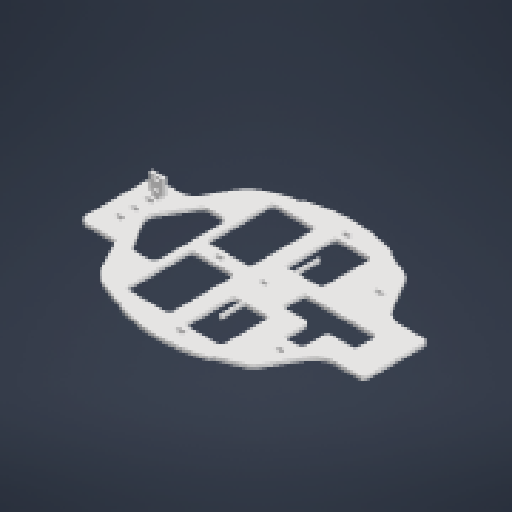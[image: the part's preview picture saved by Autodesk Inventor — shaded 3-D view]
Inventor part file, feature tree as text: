
AUTODESK INVENTOR PART (.ipt)
format: ipt  version: 2025.3 (Build 293356000, 356)  size: 523,264 bytes
history: native  units: in
note: dims shown in document units (in); Inventor stores cm internally (conversion verified against a paired STEP export)
features: extrude x3, sketch x2, projected_geometry x2, other x2, reference x1
ambient origin geometry x8: Origin, YZ Plane, XZ Plane, XY Plane, X Axis, Y Axis, Z Axis, Center Point
bodies: Solid1 (feature_tree), Solid2 (feature_tree), Body1 (feature_tree), Body2 (feature_tree)
feature tree (10):
  sketch  "Sketch1"  dims[d0=0.3937in d1=0.1969in]
  extrude  "Extrusion1"  Depth=0.1969in
  extrude  "Extrusion2"  Depth=0.3937in TaperAngle=0.0deg
  extrude  "Extrusion3"  Depth=0.3937in TaperAngle=0.0deg
  projected_geometry  "Projected Loop1"
  sketch  "Sketch2"  dims[d2=0.3937in d3=0.3937in d4=0.0in d5=0.3937in d6=0.0in d7=0.1575in d8=2.7559in d9=0.3937in d10=0.0in]
  reference  "Reference1"
  projected_geometry  "Projected Loop2"
  other  "Assembly2.iam"
  other  "base botellas:1"
